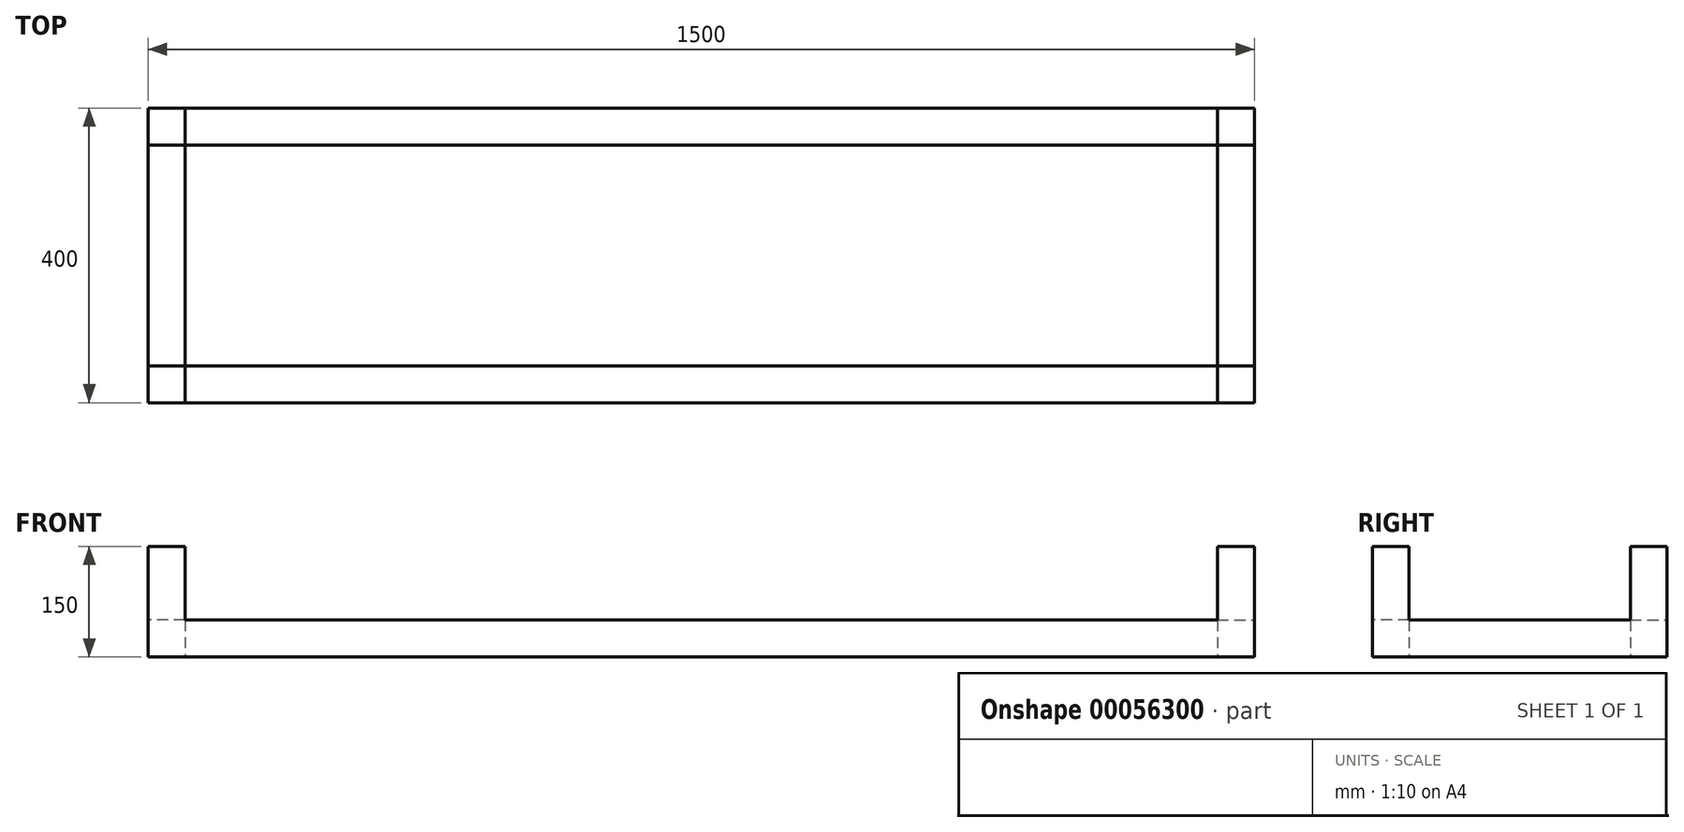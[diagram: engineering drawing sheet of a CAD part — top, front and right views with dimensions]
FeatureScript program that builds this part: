
annotation { "Feature Type Name" : "Feature", "Feature Type Description" : "" }
export const myFeature = defineFeature(function(context is Context, id is Id, definition is map)
    precondition{}
    {
        {
            var Q0;
            Q0=qCreatedBy(makeId("Top.planeOp"),FACE);
            var sketch = newSketch(context, id + "F0", { "sketchPlane" : qUnion([Q0])});
            skLineSegment(sketch, "E0.bottom", {"start": v(0, 400) * mm, "end": v(1500, 400) * mm});
            skLineSegment(sketch, "E0.top", {"start": v(0, 0) * mm, "end": v(1500, 0) * mm});
            skLineSegment(sketch, "E0.left", {"start": v(0, 400) * mm, "end": v(0, 0) * mm});
            skLineSegment(sketch, "E0.right", {"start": v(1500, 400) * mm, "end": v(1500, 0) * mm});
            skLineSegment(sketch, "E1.0", {"start": v(50, 350) * mm, "end": v(1450, 350) * mm});
            skLineSegment(sketch, "E1.1", {"start": v(50, 350) * mm, "end": v(50, 50) * mm});
            skLineSegment(sketch, "E1.2", {"start": v(50, 50) * mm, "end": v(1450, 50) * mm});
            skLineSegment(sketch, "E1.3", {"start": v(1450, 350) * mm, "end": v(1450, 50) * mm});
            skSolve(sketch);
        }
        {
            var Q0;
            Q0=makeQuery(id+"F0.imprint","IMPRINT",FACE,{"disambiguationData":[TD([[makeQuery(id+"F0.imprint","IMPRINT",EDGE,{"derivedFrom":sQuery(id+"F0.wireOp",EDGE,"E0.bottom")}),-1.0]])]});
            extrude(context, id + "F1", {"entities" : qUnion([Q0]), "depth" : 50 * mm});
        }
        {
            var Q0;
            Q0=makeQuery(id+"F1.opExtrude","CAP_FACE",FACE,{"disambiguationData":[OSD([sQuery(id+"F0.wireOp",EDGE,"E0.bottom"),sQuery(id+"F0.wireOp",EDGE,"E0.top"),sQuery(id+"F0.wireOp",EDGE,"E0.left"),sQuery(id+"F0.wireOp",EDGE,"E0.right"),sQuery(id+"F0.wireOp",EDGE,"E1.0"),sQuery(id+"F0.wireOp",EDGE,"E1.1"),sQuery(id+"F0.wireOp",EDGE,"E1.2"),sQuery(id+"F0.wireOp",EDGE,"E1.3")])],"isStart":false});
            var sketch = newSketch(context, id + "F2", { "sketchPlane" : qUnion([Q0])});
            skLineSegment(sketch, "E2.bottom", {"start": v(0, 400) * mm, "end": v(50, 400) * mm});
            skLineSegment(sketch, "E2.top", {"start": v(0, 350) * mm, "end": v(50, 350) * mm});
            skLineSegment(sketch, "E2.left", {"start": v(0, 400) * mm, "end": v(0, 350) * mm});
            skLineSegment(sketch, "E2.right", {"start": v(50, 400) * mm, "end": v(50, 350) * mm});
            skLineSegment(sketch, "E3.bottom", {"start": v(50, 50) * mm, "end": v(0, 50) * mm});
            skLineSegment(sketch, "E3.top", {"start": v(50, 0) * mm, "end": v(0, 0) * mm});
            skLineSegment(sketch, "E3.left", {"start": v(50, 50) * mm, "end": v(50, 0) * mm});
            skLineSegment(sketch, "E3.right", {"start": v(0, 50) * mm, "end": v(0, 0) * mm});
            skLineSegment(sketch, "E4.bottom", {"start": v(1450, 350) * mm, "end": v(1500, 350) * mm});
            skLineSegment(sketch, "E4.top", {"start": v(1450, 400) * mm, "end": v(1500, 400) * mm});
            skLineSegment(sketch, "E4.left", {"start": v(1450, 350) * mm, "end": v(1450, 400) * mm});
            skLineSegment(sketch, "E4.right", {"start": v(1500, 350) * mm, "end": v(1500, 400) * mm});
            skLineSegment(sketch, "E5.bottom", {"start": v(1450, 50) * mm, "end": v(1500, 50) * mm});
            skLineSegment(sketch, "E5.top", {"start": v(1450, 0) * mm, "end": v(1500, 0) * mm});
            skLineSegment(sketch, "E5.left", {"start": v(1450, 50) * mm, "end": v(1450, 0) * mm});
            skLineSegment(sketch, "E5.right", {"start": v(1500, 50) * mm, "end": v(1500, 0) * mm});
            skSolve(sketch);
        }
        {
            var Q0;
            Q0 = qSketchRegion(id + "F2", true);
            extrude(context, id + "F3", {"entities" : qUnion([Q0]), "operationType" : NewBodyOperationType.ADD, "depth" : 100 * mm});
        }
    });
